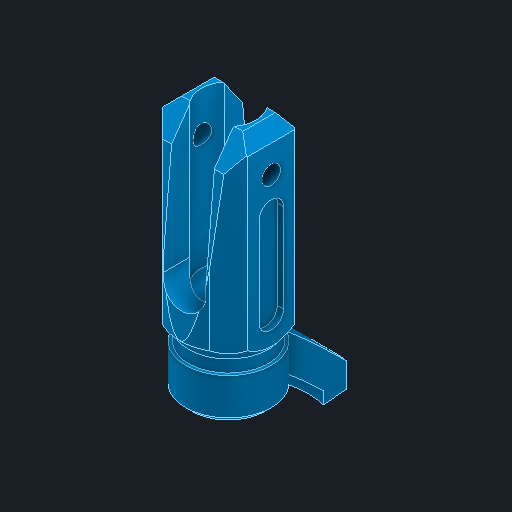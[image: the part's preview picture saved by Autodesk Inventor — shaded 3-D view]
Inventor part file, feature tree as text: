
AUTODESK INVENTOR PART (.ipt)
format: ipt  version: 2023.2 (Build 272271000, 271)  size: 442,368 bytes
history: native  units: mm
features: sketch x11, extrude x10, chamfer x3, hole x2, revolve x1, mirror x1
ambient origin geometry x8: Origin, YZ Plane, XZ Plane, XY Plane, X Axis, Y Axis, Z Axis, Center Point
bodies: Volumenkörper1 (feature_tree)
feature tree (28):
  sketch  "Skizze1"  dims[d0=14.0mm d1=7.0mm d2=0.0mm]
  extrude  "Extrusion1"  Depth=7.0mm TaperAngle=0.0deg
  chamfer  "Fase1"  Distance=4.0mm
  extrude  "Extrusion2"  Depth=16.0mm
  extrude  "Extrusion3"  Depth=1.5mm TaperAngle=45.0deg
  extrude  "Extrusion7"  TaperAngle=0.0deg  [1 undecoded]
  chamfer  "Fase2"  [1 undecoded]
  extrude  "Extrusion4"  TaperAngle=135.0deg  [1 undecoded]
  extrude  "Extrusion5"  TaperAngle=135.0deg  [1 undecoded]
  extrude  "Extrusion6"  Depth=8.0mm
  revolve  "Umdrehung2"
  extrude  "Extrusion12"  Depth=8.0mm
  chamfer  "Fase4"  Distance=0.872665mm
  hole  "Bohrung1"  [1 undecoded]
  extrude  "Extrusion13"  Depth=8.0mm
  mirror  "Spiegeln1"
  hole  "Bohrung2"  [1 undecoded]
  extrude  "Extrusion14"  Depth=8.0mm
  sketch  "Skizze2"  dims[d3=13.0mm d4=4.0mm d5=0.0mm]
  sketch  "Skizze3"  dims[d6=1.0mm d7=2.0mm d8=45.0deg d9=16.0mm]
  sketch  "Skizze5"  dims[d10=29.5mm d11=0.0mm d12=1.5mm d13=2.0mm d14=45.0deg]
  sketch  "Skizze6"  dims[d15=14.0mm d19=0.0mm d20=0.0mm]
  sketch  "Skizze11"  dims[d26=7.0mm]
  sketch  "Skizze16"  dims[d28=22.0mm]
  sketch  "Skizze17"  dims[d29=9.5mm d30=0.0mm d31=0.0mm]
  sketch  "Skizze18"  dims[d33=135.0deg d34=135.0deg]
  sketch  "Skizze19"  dims[d35=135.0deg d36=135.0deg]
  sketch  "Skizze20"  dims[d39=25.0mm d42=0.872665mm d43=25.0mm d44=0.872665mm d46=0.0mm d47=0.0mm d48=7.0mm d49=14.0mm d51=7.0mm d52=6.108652mm d53=6.108652mm d54=4.0mm d55=0.0mm d56=0.0mm d64=135.0deg d67=2.0mm d78=90.0deg d79=3.5mm d80=2.5mm d83=14.0mm d84=0.0mm d88=2.0mm d89=2.0mm d90=45.0deg d91=3.0mm d92=6.0mm d93=4.0mm d94=2.0mm d95=90.0deg d96=8.0mm d97=20.594885mm d100=4.5mm d101=7.0mm d102=14.0mm d103=4.0mm d104=7.0mm d105=10.0mm d106=4.0mm d107=14.5mm d108=1.0mm d109=0.0mm d110=2.0mm d111=6.0mm d112=4.0mm d113=2.0mm d114=90.0deg d115=8.0mm d116=20.594885mm d117=15.0mm d118=0.0mm d119=9.0mm d120=25.5mm d121=0.0mm d122=2.0mm d68=0.5mm d69=0.872665mm d70=0.5mm d71=0.872665mm d85=0.5mm d86=0.872665mm]
note: 6 required parameter values undecoded (feature->parameter linkage not recoverable at this tier; creation-order binding heuristic only, values carry confidence <= 0.55)
